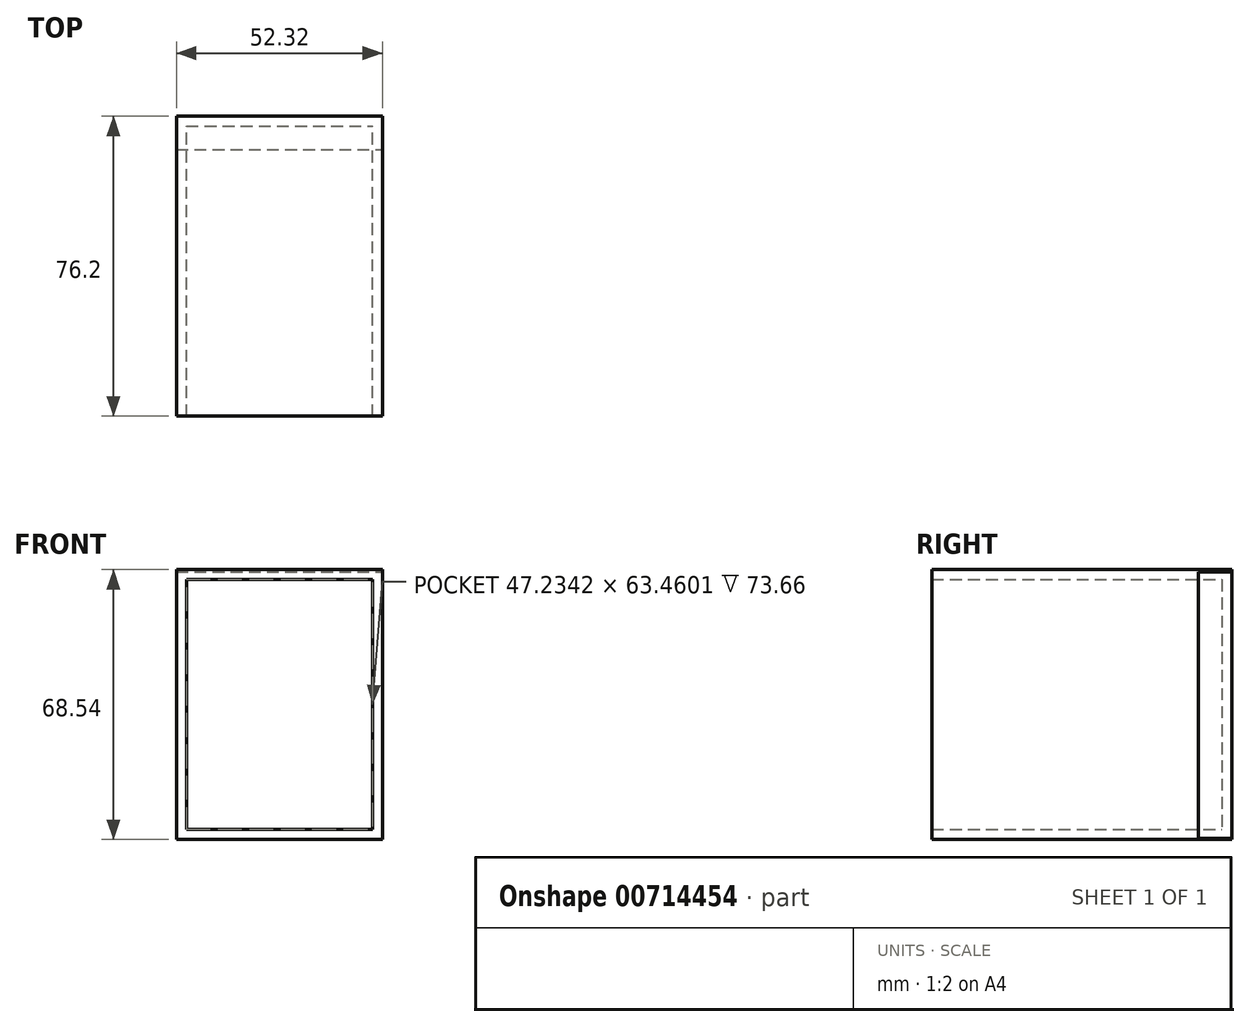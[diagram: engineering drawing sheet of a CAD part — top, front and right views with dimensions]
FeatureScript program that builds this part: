
annotation { "Feature Type Name" : "Feature", "Feature Type Description" : "" }
export const myFeature = defineFeature(function(context is Context, id is Id, definition is map)
    precondition{}
    {
        {
            var Q0;
            Q0=qCreatedBy(makeId("Front.planeOp"),FACE);
            var sketch = newSketch(context, id + "F0", { "sketchPlane" : qUnion([Q0])});
            skLineSegment(sketch, "E0.bottom", {"start": v(-24.48, 36.5) * mm, "end": v(27.84, 36.5) * mm});
            skLineSegment(sketch, "E0.top", {"start": v(-24.48, -32.03) * mm, "end": v(27.84, -32.03) * mm});
            skLineSegment(sketch, "E1", {"start": v(-24.48, 36.5) * mm, "end": v(-24.48, -32.03) * mm});
            skLineSegment(sketch, "E2", {"start": v(27.84, 36.5) * mm, "end": v(27.84, -32.03) * mm});
            skSolve(sketch);
        }
        {
            var Q0;
            Q0=makeQuery(id+"F0.imprint","IMPRINT",FACE,{"disambiguationData":[TD([[makeQuery(id+"F0.imprint","IMPRINT",EDGE,{"derivedFrom":sQuery(id+"F0.wireOp",EDGE,"E0.bottom")}),-1.0]])]});
            extrude(context, id + "F1", {"entities" : qUnion([Q0]), "depth" : 76.2 * mm, "offsetDistance" : 25.4 * mm});
        }
        {
            var Q0;
            Q0=makeQuery(id+"F1.opExtrude","CAP_FACE",FACE,{"disambiguationData":[OSD([sQuery(id+"F0.wireOp",EDGE,"E0.bottom"),sQuery(id+"F0.wireOp",EDGE,"E0.top"),sQuery(id+"F0.wireOp",EDGE,"E1"),sQuery(id+"F0.wireOp",EDGE,"E2")])],"isStart":false});
            shell(context, id + "F2", {"entities" : qUnion([Q0]), "thickness" : 2.54 * mm});
        }
        {
            var Q0;
            Q0=qCreatedBy(makeId("Front.planeOp"),FACE);
            var sketch = newSketch(context, id + "F3", { "sketchPlane" : qUnion([Q0])});
            skLineSegment(sketch, "E3.bottom", {"start": v(-24.48, 35.95) * mm, "end": v(27.84, 35.95) * mm});
            skLineSegment(sketch, "E3.top", {"start": v(-24.48, -31.75) * mm, "end": v(27.84, -31.75) * mm});
            skLineSegment(sketch, "E3.left", {"start": v(-24.48, 35.95) * mm, "end": v(-24.48, -31.75) * mm});
            skLineSegment(sketch, "E3.right", {"start": v(27.84, 35.95) * mm, "end": v(27.84, -31.75) * mm});
            skSolve(sketch);
        }
        {
            var Q0;
            Q0=makeQuery(id+"F3.imprint","IMPRINT",FACE,{"disambiguationData":[TD([[makeQuery(id+"F3.imprint","IMPRINT",EDGE,{"derivedFrom":sQuery(id+"F3.wireOp",EDGE,"E3.bottom")}),-1.0]])]});
            extrude(context, id + "F4", {"entities" : qUnion([Q0]), "depth" : 8.47 * mm, "offsetDistance" : 25.4 * mm});
        }
    });
